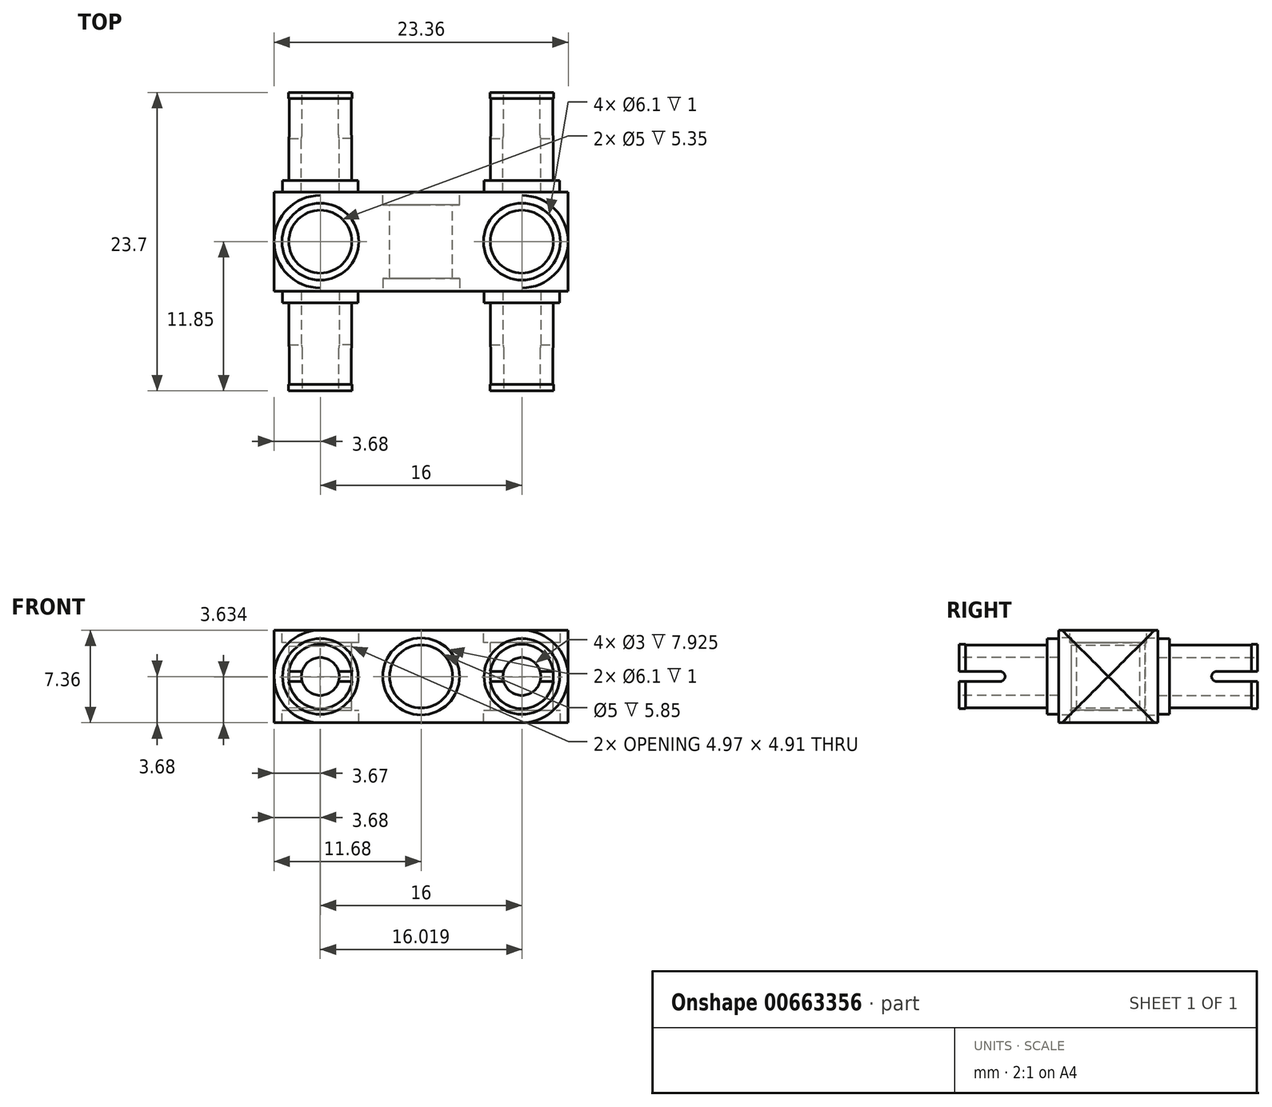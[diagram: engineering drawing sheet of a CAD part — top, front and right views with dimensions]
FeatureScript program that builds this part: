
annotation { "Feature Type Name" : "Feature", "Feature Type Description" : "" }
export const myFeature = defineFeature(function(context is Context, id is Id, definition is map)
    precondition{}
    {
        {
            var Q0;
            Q0=qCreatedBy(makeId("Front.planeOp"),FACE);
            var sketch = newSketch(context, id + "F0", { "sketchPlane" : qUnion([Q0])});
            skLineSegment(sketch, "E0.bottom", {"start": v(11.68, 3.67) * mm, "end": v(-11.68, 3.67) * mm});
            skLineSegment(sketch, "E0.top", {"start": v(11.68, -3.67) * mm, "end": v(-11.68, -3.67) * mm});
            skLineSegment(sketch, "E0.left", {"start": v(11.68, 3.67) * mm, "end": v(11.68, -3.67) * mm});
            skLineSegment(sketch, "E0.right", {"start": v(-11.68, 3.67) * mm, "end": v(-11.68, -3.67) * mm});
            skPoint(sketch, "E0.middle", {"position": v(0, 0) * mm});
            skCircle(sketch, "E1", {"center": v(-8, 0) * mm, "radius": 3.67 * mm});
            skCircle(sketch, "E2", {"center": v(8, 0) * mm, "radius": 3.67 * mm});
            skCircle(sketch, "E3", {"center": v(0, 0) * mm, "radius": 2.5 * mm});
            skCircle(sketch, "E4", {"center": v(0, 0) * mm, "radius": 3.05 * mm});
            skCircle(sketch, "E5", {"center": v(-8, 0) * mm, "radius": 3 * mm});
            skCircle(sketch, "E6", {"center": v(8, 0) * mm, "radius": 3 * mm});
            skCircle(sketch, "E7", {"center": v(-8, 0) * mm, "radius": 2.5 * mm});
            skCircle(sketch, "E8", {"center": v(8, 0) * mm, "radius": 2.5 * mm});
            skSolve(sketch);
        }
        {
            var Q0;
            Q0=makeQuery(id+"F0.imprint","IMPRINT",FACE,{"disambiguationData":[TD([[makeQuery(id+"F0.imprint","IMPRINT",EDGE,{"derivedFrom":sQuery(id+"F0.wireOp",EDGE,"E4")}),-1.0]])]});
            var Q1;
            {var subQ0=sQuery(id+"F0.wireOp",EDGE,"E1");var subQ1=makeQuery(id+"F0.imprint","INTERSECT",VERTEX,{"derivedFrom":[sQuery(id+"F0.wireOp",EDGE,"E0.bottom"),subQ0]});Q1=makeQuery(id+"F0.imprint","IMPRINT",FACE,{"disambiguationData":[TD([[makeQuery(id+"F0.imprint","IMPRINT",EDGE,{"disambiguationData":[TD([[subQ1,-1.0]])],"derivedFrom":subQ0}),1.0]])]});}
            var Q2;
            {var subQ0=sQuery(id+"F0.wireOp",EDGE,"E2");var subQ1=makeQuery(id+"F0.imprint","INTERSECT",VERTEX,{"derivedFrom":[sQuery(id+"F0.wireOp",EDGE,"E0.bottom"),subQ0]});Q2=makeQuery(id+"F0.imprint","IMPRINT",FACE,{"disambiguationData":[TD([[makeQuery(id+"F0.imprint","IMPRINT",EDGE,{"disambiguationData":[TD([[subQ1,1.0]])],"derivedFrom":subQ0}),1.0]])]});}
            var Q3;
            Q3=makeQuery(id+"F0.imprint","IMPRINT",FACE,{"disambiguationData":[TD([[makeQuery(id+"F0.imprint","IMPRINT",EDGE,{"derivedFrom":sQuery(id+"F0.wireOp",EDGE,"E3")}),-1.0]])]});
            extrude(context, id + "F1", {"entities" : qUnion([Q0, Q1, Q2, Q3]), "endBound" : BoundingType.SYMMETRIC, "depth" : 7.85 * mm, "offsetDistance" : 25 * mm});
        }
        {
            var Q0;
            Q0=makeQuery(id+"F0.imprint","IMPRINT",FACE,{"disambiguationData":[TD([[makeQuery(id+"F0.imprint","IMPRINT",EDGE,{"derivedFrom":sQuery(id+"F0.wireOp",EDGE,"E5")}),1.0]])]});
            var Q1;
            Q1=makeQuery(id+"F0.imprint","IMPRINT",FACE,{"disambiguationData":[TD([[makeQuery(id+"F0.imprint","IMPRINT",EDGE,{"derivedFrom":sQuery(id+"F0.wireOp",EDGE,"E6")}),1.0]])]});
            extrude(context, id + "F2", {"entities" : qUnion([Q0, Q1]), "operationType" : NewBodyOperationType.ADD, "endBound" : BoundingType.SYMMETRIC, "depth" : 9.7 * mm, "offsetDistance" : 25 * mm});
        }
        {
            var Q0;
            Q0=makeQuery(id+"F0.imprint","IMPRINT",FACE,{"disambiguationData":[TD([[makeQuery(id+"F0.imprint","IMPRINT",EDGE,{"derivedFrom":sQuery(id+"F0.wireOp",EDGE,"E7")}),1.0]])]});
            var Q1;
            Q1=makeQuery(id+"F0.imprint","IMPRINT",FACE,{"disambiguationData":[TD([[makeQuery(id+"F0.imprint","IMPRINT",EDGE,{"derivedFrom":sQuery(id+"F0.wireOp",EDGE,"E8")}),1.0]])]});
            extrude(context, id + "F3", {"entities" : qUnion([Q0, Q1]), "operationType" : NewBodyOperationType.ADD, "endBound" : BoundingType.SYMMETRIC, "depth" : 22.5 * mm, "offsetDistance" : 25 * mm});
        }
        {
            var Q0;
            Q0=makeQuery(id+"F3.opExtrude","CAP_FACE",FACE,{"disambiguationData":[OSD([sQuery(id+"F0.wireOp",EDGE,"E7")])],"isStart":false});
            var sketch = newSketch(context, id + "F4", { "sketchPlane" : qUnion([Q0])});
            skCircle(sketch, "E9", {"center": v(-8, 0) * mm, "radius": 2.55 * mm});
            skSolve(sketch);
        }
        {
            var Q0;
            Q0=qSketchRegion(id+"F4",true);
            extrude(context, id + "F5", {"entities" : qUnion([Q0]), "operationType" : NewBodyOperationType.ADD, "depth" : 0.6 * mm, "offsetDistance" : 25 * mm});
        }
        {
            var Q0;
            Q0=makeQuery(id+"F3.opExtrude","CAP_FACE",FACE,{"disambiguationData":[OSD([sQuery(id+"F0.wireOp",EDGE,"E8")])],"isStart":false});
            var sketch = newSketch(context, id + "F6", { "sketchPlane" : qUnion([Q0])});
            skCircle(sketch, "E10", {"center": v(8, 0) * mm, "radius": 2.55 * mm});
            skSolve(sketch);
        }
        {
            var Q0;
            Q0=qSketchRegion(id+"F6",true);
            extrude(context, id + "F7", {"entities" : qUnion([Q0]), "operationType" : NewBodyOperationType.ADD, "depth" : 0.6 * mm, "offsetDistance" : 25 * mm});
        }
        {
            var Q0;
            Q0=makeQuery(id+"F3.opExtrude","CAP_FACE",FACE,{"disambiguationData":[OSD([sQuery(id+"F0.wireOp",EDGE,"E7")])],"isStart":true});
            var sketch = newSketch(context, id + "F8", { "sketchPlane" : qUnion([Q0])});
            skCircle(sketch, "E11", {"center": v(8, 0) * mm, "radius": 2.55 * mm});
            skSolve(sketch);
        }
        {
            var Q0;
            Q0=qSketchRegion(id+"F8",true);
            extrude(context, id + "F9", {"entities" : qUnion([Q0]), "operationType" : NewBodyOperationType.ADD, "depth" : 0.6 * mm, "offsetDistance" : 25 * mm});
        }
        {
            var Q0;
            Q0=makeQuery(id+"F3.opExtrude","CAP_FACE",FACE,{"disambiguationData":[OSD([sQuery(id+"F0.wireOp",EDGE,"E8")])],"isStart":true});
            var sketch = newSketch(context, id + "F10", { "sketchPlane" : qUnion([Q0])});
            skCircle(sketch, "E12", {"center": v(-8, 0) * mm, "radius": 2.55 * mm});
            skSolve(sketch);
        }
        {
            var Q0;
            Q0=qSketchRegion(id+"F10",true);
            extrude(context, id + "F11", {"entities" : qUnion([Q0]), "operationType" : NewBodyOperationType.ADD, "depth" : 0.6 * mm, "offsetDistance" : 25 * mm});
        }
        {
            var Q0;
            Q0=makeQuery(id+"F9.opExtrude","CAP_FACE",FACE,{"disambiguationData":[OSD([sQuery(id+"F8.wireOp",EDGE,"E11")])],"isStart":false});
            var sketch = newSketch(context, id + "F12", { "sketchPlane" : qUnion([Q0])});
            skCircle(sketch, "E13", {"center": v(8, 0) * mm, "radius": 1.5 * mm});
            skSolve(sketch);
        }
        {
            var Q0;
            Q0=qSketchRegion(id+"F12",true);
            var Q1;
            Q1=makeQuery(id+"F1.opExtrude","CAP_FACE",FACE,{"disambiguationData":[OSD([sQuery(id+"F0.wireOp",EDGE,"E0.bottom"),sQuery(id+"F0.wireOp",EDGE,"E0.top"),sQuery(id+"F0.wireOp",EDGE,"E1"),sQuery(id+"F0.wireOp",EDGE,"E2"),sQuery(id+"F0.wireOp",EDGE,"E3"),sQuery(id+"F0.wireOp",EDGE,"E5"),sQuery(id+"F0.wireOp",EDGE,"E6")])],"isStart":true});
            extrude(context, id + "F13", {"entities" : qUnion([Q0]), "operationType" : NewBodyOperationType.REMOVE, "endBound" : BoundingType.UP_TO_SURFACE, "oppositeDirection" : true, "depth" : 25 * mm, "endBoundEntityFace" : qUnion([Q1]), "offsetDistance" : 25 * mm});
        }
        {
            var Q0;
            Q0=makeQuery(id+"F11.opExtrude","CAP_FACE",FACE,{"disambiguationData":[OSD([sQuery(id+"F10.wireOp",EDGE,"E12")])],"isStart":false});
            var sketch = newSketch(context, id + "F14", { "sketchPlane" : qUnion([Q0])});
            skCircle(sketch, "E14", {"center": v(-8, 0) * mm, "radius": 1.5 * mm});
            skSolve(sketch);
        }
        {
            var Q0;
            Q0=qSketchRegion(id+"F14",true);
            var Q1;
            Q1=makeQuery(id+"F1.opExtrude","CAP_FACE",FACE,{"disambiguationData":[OSD([sQuery(id+"F0.wireOp",EDGE,"E0.bottom"),sQuery(id+"F0.wireOp",EDGE,"E0.top"),sQuery(id+"F0.wireOp",EDGE,"E1"),sQuery(id+"F0.wireOp",EDGE,"E2"),sQuery(id+"F0.wireOp",EDGE,"E3"),sQuery(id+"F0.wireOp",EDGE,"E5"),sQuery(id+"F0.wireOp",EDGE,"E6")])],"isStart":true});
            extrude(context, id + "F15", {"entities" : qUnion([Q0]), "operationType" : NewBodyOperationType.REMOVE, "endBound" : BoundingType.UP_TO_SURFACE, "oppositeDirection" : true, "depth" : 25 * mm, "endBoundEntityFace" : qUnion([Q1]), "offsetDistance" : 25 * mm});
        }
        {
            var Q0;
            Q0=makeQuery(id+"F7.opExtrude","CAP_FACE",FACE,{"disambiguationData":[OSD([sQuery(id+"F6.wireOp",EDGE,"E10")])],"isStart":false});
            var sketch = newSketch(context, id + "F16", { "sketchPlane" : qUnion([Q0])});
            skCircle(sketch, "E15", {"center": v(8, 0) * mm, "radius": 1.5 * mm});
            skSolve(sketch);
        }
        {
            var Q0;
            Q0=qSketchRegion(id+"F16",true);
            var Q1;
            Q1=makeQuery(id+"F1.opExtrude","CAP_FACE",FACE,{"disambiguationData":[OSD([sQuery(id+"F0.wireOp",EDGE,"E0.bottom"),sQuery(id+"F0.wireOp",EDGE,"E0.top"),sQuery(id+"F0.wireOp",EDGE,"E1"),sQuery(id+"F0.wireOp",EDGE,"E2"),sQuery(id+"F0.wireOp",EDGE,"E3"),sQuery(id+"F0.wireOp",EDGE,"E5"),sQuery(id+"F0.wireOp",EDGE,"E6")])],"isStart":false});
            extrude(context, id + "F17", {"entities" : qUnion([Q0]), "operationType" : NewBodyOperationType.REMOVE, "endBound" : BoundingType.UP_TO_SURFACE, "oppositeDirection" : true, "depth" : 25 * mm, "endBoundEntityFace" : qUnion([Q1]), "offsetDistance" : 25 * mm});
        }
        {
            var Q0;
            Q0=makeQuery(id+"F5.opExtrude","CAP_FACE",FACE,{"disambiguationData":[OSD([sQuery(id+"F4.wireOp",EDGE,"E9")])],"isStart":false});
            var sketch = newSketch(context, id + "F18", { "sketchPlane" : qUnion([Q0])});
            skCircle(sketch, "E16", {"center": v(-8, 0) * mm, "radius": 1.5 * mm});
            skSolve(sketch);
        }
        {
            var Q0;
            Q0=qSketchRegion(id+"F18",true);
            var Q1;
            Q1=makeQuery(id+"F1.opExtrude","CAP_FACE",FACE,{"disambiguationData":[OSD([sQuery(id+"F0.wireOp",EDGE,"E0.bottom"),sQuery(id+"F0.wireOp",EDGE,"E0.top"),sQuery(id+"F0.wireOp",EDGE,"E1"),sQuery(id+"F0.wireOp",EDGE,"E2"),sQuery(id+"F0.wireOp",EDGE,"E3"),sQuery(id+"F0.wireOp",EDGE,"E5"),sQuery(id+"F0.wireOp",EDGE,"E6")])],"isStart":false});
            extrude(context, id + "F19", {"entities" : qUnion([Q0]), "operationType" : NewBodyOperationType.REMOVE, "endBound" : BoundingType.UP_TO_SURFACE, "oppositeDirection" : true, "depth" : 25 * mm, "endBoundEntityFace" : qUnion([Q1]), "offsetDistance" : 25 * mm});
        }
        {
            var Q0;
            Q0=makeQuery(id+"F1.opExtrude","SWEPT_FACE",FACE,{"disambiguationData":[OSD([sQuery(id+"F0.wireOp",EDGE,"E0.bottom")])]});
            var sketch = newSketch(context, id + "F20", { "sketchPlane" : qUnion([Q0])});
            skCircle(sketch, "E17", {"center": v(-8, 0) * mm, "radius": 3.67 * mm});
            skCircle(sketch, "E18", {"center": v(8, 0) * mm, "radius": 3.67 * mm});
            skCircle(sketch, "E19", {"center": v(-8, 0) * mm, "radius": 2.5 * mm});
            skCircle(sketch, "E20", {"center": v(8, 0) * mm, "radius": 2.5 * mm});
            skCircle(sketch, "E21", {"center": v(-8, 0) * mm, "radius": 3.05 * mm});
            skCircle(sketch, "E22", {"center": v(8, 0) * mm, "radius": 3.05 * mm});
            skSolve(sketch);
        }
        {
            var Q0;
            Q0=qSketchRegion(id+"F20",true);
            var Q1;
            Q1=makeQuery(id+"F1.opExtrude","SWEPT_FACE",FACE,{"disambiguationData":[OSD([sQuery(id+"F0.wireOp",EDGE,"E0.top")])]});
            extrude(context, id + "F21", {"entities" : qUnion([Q0]), "operationType" : NewBodyOperationType.ADD, "endBound" : BoundingType.UP_TO_SURFACE, "oppositeDirection" : true, "depth" : 25 * mm, "endBoundEntityFace" : qUnion([Q1]), "offsetDistance" : 25 * mm});
        }
        {
            var Q0;
            {var subQ0=sQuery(id+"F20.wireOp",EDGE,"E19");var subQ1=makeQuery(id+"F1.opExtrude","SWEPT_EDGE",EDGE,{"disambiguationData":[OSD([sQuery(id+"F0.wireOp",EDGE,"E0.bottom"),sQuery(id+"F0.wireOp",EDGE,"E1")])]});var subQ2=makeQuery(id+"F20.imprint","INTERSECT",VERTEX,{"disambiguationData":[OD(0.0)],"derivedFrom":[subQ1,subQ0]});Q0=makeQuery(id+"F20.imprint","IMPRINT",FACE,{"disambiguationData":[TD([[makeQuery(id+"F20.imprint","IMPRINT",EDGE,{"disambiguationData":[TD([[subQ2,-1.0]])],"derivedFrom":subQ0}),1.0]])]});}
            var Q1;
            {var subQ0=sQuery(id+"F20.wireOp",EDGE,"E19");var subQ1=makeQuery(id+"F1.opExtrude","SWEPT_EDGE",EDGE,{"disambiguationData":[OSD([sQuery(id+"F0.wireOp",EDGE,"E0.bottom"),sQuery(id+"F0.wireOp",EDGE,"E1")])]});var subQ2=makeQuery(id+"F20.imprint","INTERSECT",VERTEX,{"disambiguationData":[OD(0.0)],"derivedFrom":[subQ1,subQ0]});Q1=makeQuery(id+"F20.imprint","IMPRINT",FACE,{"disambiguationData":[TD([[makeQuery(id+"F20.imprint","IMPRINT",EDGE,{"disambiguationData":[TD([[subQ2,1.0]])],"derivedFrom":subQ0}),1.0]])]});}
            var Q2;
            {var subQ0=sQuery(id+"F20.wireOp",EDGE,"E20");var subQ1=makeQuery(id+"F1.opExtrude","SWEPT_EDGE",EDGE,{"disambiguationData":[OSD([sQuery(id+"F0.wireOp",EDGE,"E0.bottom"),sQuery(id+"F0.wireOp",EDGE,"E2")])]});var subQ2=makeQuery(id+"F20.imprint","INTERSECT",VERTEX,{"disambiguationData":[OD(0.0)],"derivedFrom":[subQ1,subQ0]});Q2=makeQuery(id+"F20.imprint","IMPRINT",FACE,{"disambiguationData":[TD([[makeQuery(id+"F20.imprint","IMPRINT",EDGE,{"disambiguationData":[TD([[subQ2,-1.0]])],"derivedFrom":subQ0}),1.0]])]});}
            var Q3;
            {var subQ0=sQuery(id+"F20.wireOp",EDGE,"E20");var subQ1=makeQuery(id+"F1.opExtrude","SWEPT_EDGE",EDGE,{"disambiguationData":[OSD([sQuery(id+"F0.wireOp",EDGE,"E0.bottom"),sQuery(id+"F0.wireOp",EDGE,"E2")])]});var subQ2=makeQuery(id+"F20.imprint","INTERSECT",VERTEX,{"disambiguationData":[OD(0.0)],"derivedFrom":[subQ1,subQ0]});Q3=makeQuery(id+"F20.imprint","IMPRINT",FACE,{"disambiguationData":[TD([[makeQuery(id+"F20.imprint","IMPRINT",EDGE,{"disambiguationData":[TD([[subQ2,1.0]])],"derivedFrom":subQ0}),1.0]])]});}
            extrude(context, id + "F22", {"entities" : qUnion([Q0, Q1, Q2, Q3]), "operationType" : NewBodyOperationType.REMOVE, "endBound" : BoundingType.THROUGH_ALL, "oppositeDirection" : true, "depth" : 25 * mm, "offsetDistance" : 25 * mm});
        }
        {
            var Q0;
            {var subQ0=sQuery(id+"F20.wireOp",EDGE,"E19");var subQ1=makeQuery(id+"F1.opExtrude","SWEPT_EDGE",EDGE,{"disambiguationData":[OSD([sQuery(id+"F0.wireOp",EDGE,"E0.bottom"),sQuery(id+"F0.wireOp",EDGE,"E1")])]});var subQ2=makeQuery(id+"F20.imprint","INTERSECT",VERTEX,{"disambiguationData":[OD(0.0)],"derivedFrom":[subQ1,subQ0]});Q0=makeQuery(id+"F20.imprint","IMPRINT",FACE,{"disambiguationData":[TD([[makeQuery(id+"F20.imprint","IMPRINT",EDGE,{"disambiguationData":[TD([[subQ2,1.0]])],"derivedFrom":subQ0}),-1.0]])]});}
            var Q1;
            {var subQ0=sQuery(id+"F20.wireOp",EDGE,"E20");var subQ1=makeQuery(id+"F1.opExtrude","SWEPT_EDGE",EDGE,{"disambiguationData":[OSD([sQuery(id+"F0.wireOp",EDGE,"E0.bottom"),sQuery(id+"F0.wireOp",EDGE,"E2")])]});var subQ2=makeQuery(id+"F20.imprint","INTERSECT",VERTEX,{"disambiguationData":[OD(0.0)],"derivedFrom":[subQ1,subQ0]});Q1=makeQuery(id+"F20.imprint","IMPRINT",FACE,{"disambiguationData":[TD([[makeQuery(id+"F20.imprint","IMPRINT",EDGE,{"disambiguationData":[TD([[subQ2,-1.0]])],"derivedFrom":subQ0}),-1.0]])]});}
            var Q2;
            {var subQ0=sQuery(id+"F20.wireOp",EDGE,"E20");var subQ1=makeQuery(id+"F1.opExtrude","SWEPT_EDGE",EDGE,{"disambiguationData":[OSD([sQuery(id+"F0.wireOp",EDGE,"E0.bottom"),sQuery(id+"F0.wireOp",EDGE,"E2")])]});var subQ2=makeQuery(id+"F20.imprint","INTERSECT",VERTEX,{"disambiguationData":[OD(0.0)],"derivedFrom":[subQ1,subQ0]});Q2=makeQuery(id+"F20.imprint","IMPRINT",FACE,{"disambiguationData":[TD([[makeQuery(id+"F20.imprint","IMPRINT",EDGE,{"disambiguationData":[TD([[subQ2,1.0]])],"derivedFrom":subQ0}),-1.0]])]});}
            var Q3;
            {var subQ0=sQuery(id+"F20.wireOp",EDGE,"E19");var subQ1=makeQuery(id+"F1.opExtrude","SWEPT_EDGE",EDGE,{"disambiguationData":[OSD([sQuery(id+"F0.wireOp",EDGE,"E0.bottom"),sQuery(id+"F0.wireOp",EDGE,"E1")])]});var subQ2=makeQuery(id+"F20.imprint","INTERSECT",VERTEX,{"disambiguationData":[OD(0.0)],"derivedFrom":[subQ1,subQ0]});Q3=makeQuery(id+"F20.imprint","IMPRINT",FACE,{"disambiguationData":[TD([[makeQuery(id+"F20.imprint","IMPRINT",EDGE,{"disambiguationData":[TD([[subQ2,-1.0]])],"derivedFrom":subQ0}),-1.0]])]});}
            extrude(context, id + "F23", {"entities" : qUnion([Q0, Q1, Q2, Q3]), "operationType" : NewBodyOperationType.REMOVE, "oppositeDirection" : true, "depth" : 1 * mm, "offsetDistance" : 25 * mm});
        }
        {
            var Q0;
            {var subQ0=sQuery(id+"F0.wireOp",EDGE,"E0.top");Q0=makeQuery(id+"F21.boolean.opBoolean","MERGE",FACE,{"derivedFrom":[makeQuery(id+"F1.opExtrude","SWEPT_FACE",FACE,{"disambiguationData":[OSD([subQ0])]}),makeQuery(id+"F21.opExtrude","CAP_FACE",FACE,{"disambiguationData":[OSD([subQ0]),OD(0.0)],"isStart":false}),makeQuery(id+"F21.opExtrude","CAP_FACE",FACE,{"disambiguationData":[OSD([subQ0]),OD(1.0)],"isStart":false})]});}
            var sketch = newSketch(context, id + "F24", { "sketchPlane" : qUnion([Q0])});
            skCircle(sketch, "E23", {"center": v(-8, 0) * mm, "radius": 3.05 * mm});
            skCircle(sketch, "E24", {"center": v(-8, 0) * mm, "radius": 2.5 * mm});
            skCircle(sketch, "E25", {"center": v(8, 0) * mm, "radius": 2.5 * mm});
            skCircle(sketch, "E26", {"center": v(8, 0) * mm, "radius": 3.05 * mm});
            skSolve(sketch);
        }
        {
            var Q0;
            Q0=makeQuery(id+"F24.imprint","IMPRINT",FACE,{"disambiguationData":[TD([[makeQuery(id+"F24.imprint","IMPRINT",EDGE,{"disambiguationData":[OD(0.0)],"derivedFrom":sQuery(id+"F24.wireOp",EDGE,"E26")}),1.0]])]});
            var Q1;
            Q1=makeQuery(id+"F24.imprint","IMPRINT",FACE,{"disambiguationData":[TD([[makeQuery(id+"F24.imprint","IMPRINT",EDGE,{"disambiguationData":[OD(1.0)],"derivedFrom":sQuery(id+"F24.wireOp",EDGE,"E26")}),-1.0]])]});
            var Q2;
            Q2=makeQuery(id+"F24.imprint","IMPRINT",FACE,{"disambiguationData":[TD([[makeQuery(id+"F24.imprint","IMPRINT",EDGE,{"disambiguationData":[OD(1.0)],"derivedFrom":sQuery(id+"F24.wireOp",EDGE,"E23")}),-1.0]])]});
            var Q3;
            Q3=makeQuery(id+"F24.imprint","IMPRINT",FACE,{"disambiguationData":[TD([[makeQuery(id+"F24.imprint","IMPRINT",EDGE,{"disambiguationData":[OD(0.0)],"derivedFrom":sQuery(id+"F24.wireOp",EDGE,"E23")}),1.0]])]});
            extrude(context, id + "F25", {"entities" : qUnion([Q0, Q1, Q2, Q3]), "operationType" : NewBodyOperationType.REMOVE, "oppositeDirection" : true, "depth" : 1 * mm, "offsetDistance" : 25 * mm});
        }
        {
            var Q0;
            Q0=makeQuery(id+"F1.opExtrude","CAP_FACE",FACE,{"disambiguationData":[OSD([sQuery(id+"F0.wireOp",EDGE,"E0.bottom"),sQuery(id+"F0.wireOp",EDGE,"E0.top"),sQuery(id+"F0.wireOp",EDGE,"E1"),sQuery(id+"F0.wireOp",EDGE,"E2"),sQuery(id+"F0.wireOp",EDGE,"E3"),sQuery(id+"F0.wireOp",EDGE,"E5"),sQuery(id+"F0.wireOp",EDGE,"E6")])],"isStart":true});
            var sketch = newSketch(context, id + "F26", { "sketchPlane" : qUnion([Q0])});
            skCircle(sketch, "E27", {"center": v(0, 0) * mm, "radius": 3.05 * mm});
            skSolve(sketch);
        }
        {
            var Q0;
            Q0=makeQuery(id+"F26.imprint","IMPRINT",FACE,{"disambiguationData":[TD([[makeQuery(id+"F26.imprint","IMPRINT",EDGE,{"derivedFrom":sQuery(id+"F26.wireOp",EDGE,"E27")}),1.0]])]});
            extrude(context, id + "F27", {"entities" : qUnion([Q0]), "operationType" : NewBodyOperationType.REMOVE, "oppositeDirection" : true, "depth" : 1 * mm, "offsetDistance" : 25 * mm});
        }
        {
            var Q0;
            Q0=makeQuery(id+"F1.opExtrude","CAP_FACE",FACE,{"disambiguationData":[OSD([sQuery(id+"F0.wireOp",EDGE,"E0.bottom"),sQuery(id+"F0.wireOp",EDGE,"E0.top"),sQuery(id+"F0.wireOp",EDGE,"E1"),sQuery(id+"F0.wireOp",EDGE,"E2"),sQuery(id+"F0.wireOp",EDGE,"E3"),sQuery(id+"F0.wireOp",EDGE,"E5"),sQuery(id+"F0.wireOp",EDGE,"E6")])],"isStart":false});
            var sketch = newSketch(context, id + "F28", { "sketchPlane" : qUnion([Q0])});
            skCircle(sketch, "E28", {"center": v(0, 0) * mm, "radius": 3.05 * mm});
            skSolve(sketch);
        }
        {
            var Q0;
            Q0=makeQuery(id+"F28.imprint","IMPRINT",FACE,{"disambiguationData":[TD([[makeQuery(id+"F28.imprint","IMPRINT",EDGE,{"derivedFrom":sQuery(id+"F28.wireOp",EDGE,"E28")}),1.0]])]});
            extrude(context, id + "F29", {"entities" : qUnion([Q0]), "operationType" : NewBodyOperationType.REMOVE, "oppositeDirection" : true, "depth" : 1 * mm, "offsetDistance" : 25 * mm});
        }
        {
            var Q0;
            Q0=makeQuery(id+"F23.boolean.opBoolean","COPY",FACE,{"derivedFrom":makeQuery(id+"F23.opExtrude","CAP_FACE",FACE,{"disambiguationData":[OSD([sQuery(id+"F20.wireOp",EDGE,"E20"),sQuery(id+"F20.wireOp",EDGE,"E22")])],"isStart":false})});
            var sketch = newSketch(context, id + "F30", { "sketchPlane" : qUnion([Q0])});
            skCircle(sketch, "E29", {"center": v(8, 0) * mm, "radius": 3.05 * mm});
            skCircle(sketch, "E30", {"center": v(8, 0) * mm, "radius": 2.5 * mm});
            skSolve(sketch);
        }
        {
            var Q0;
            Q0=makeQuery(id+"F30.imprint","IMPRINT",FACE,{"disambiguationData":[TD([[makeQuery(id+"F30.imprint","IMPRINT",EDGE,{"derivedFrom":sQuery(id+"F30.wireOp",EDGE,"E30")}),-1.0]])]});
            var Q1;
            {var subQ1=sQuery(id+"F20.wireOp",EDGE,"E22");var subQ2=makeQuery(id+"F23.boolean.opBoolean","INTERSECT",EDGE,{"derivedFrom":[makeQuery(id+"F21.boolean.opBoolean","SPLIT",FACE,{"disambiguationData":[TD([makeQuery(id+"F1.opExtrude","SWEPT_FACE",FACE,{"disambiguationData":[OSD([sQuery(id+"F0.wireOp",EDGE,"E0.bottom")])]}),makeQuery(id+"F21.opExtrude","CAP_FACE",FACE,{"disambiguationData":[OSD([sQuery(id+"F20.wireOp",EDGE,"E17"),sQuery(id+"F20.wireOp",EDGE,"E21")])],"isStart":true}),makeQuery(id+"F21.opExtrude","CAP_FACE",FACE,{"disambiguationData":[OSD([sQuery(id+"F20.wireOp",EDGE,"E18"),subQ1])],"isStart":true}),makeQuery(id+"F21.opExtrude","SWEPT_FACE",FACE,{"disambiguationData":[OSD([subQ1])]})])],"derivedFrom":makeQuery(id+"F1.opExtrude","SWEPT_FACE",FACE,{"disambiguationData":[OSD([sQuery(id+"F0.wireOp",EDGE,"E2")])]})}),makeQuery(id+"F23.opExtrude","CAP_FACE",FACE,{"disambiguationData":[OSD([sQuery(id+"F20.wireOp",EDGE,"E20"),subQ1])],"isStart":false})]});Q1=makeQuery(id+"F30.imprint","IMPRINT",FACE,{"disambiguationData":[TD([[makeQuery(id+"F30.imprint","IMPRINT",EDGE,{"derivedFrom":subQ2}),-1.0]])]});}
            var Q2;
            Q2=makeQuery(id+"F25.boolean.opBoolean","COPY",FACE,{"derivedFrom":makeQuery(id+"F25.opExtrude","CAP_FACE",FACE,{"disambiguationData":[OSD([sQuery(id+"F24.wireOp",EDGE,"E25"),sQuery(id+"F24.wireOp",EDGE,"E26")])],"isStart":false})});
            extrude(context, id + "F31", {"entities" : qUnion([Q0, Q1]), "operationType" : NewBodyOperationType.ADD, "endBound" : BoundingType.UP_TO_SURFACE, "oppositeDirection" : true, "depth" : 25 * mm, "endBoundEntityFace" : qUnion([Q2]), "offsetDistance" : 25 * mm});
        }
        {
            var Q0;
            Q0=makeQuery(id+"F23.boolean.opBoolean","COPY",FACE,{"derivedFrom":makeQuery(id+"F23.opExtrude","CAP_FACE",FACE,{"disambiguationData":[OSD([sQuery(id+"F20.wireOp",EDGE,"E19"),sQuery(id+"F20.wireOp",EDGE,"E21")])],"isStart":false})});
            var sketch = newSketch(context, id + "F32", { "sketchPlane" : qUnion([Q0])});
            skCircle(sketch, "E31", {"center": v(-8, 0) * mm, "radius": 3.05 * mm});
            skCircle(sketch, "E32", {"center": v(-8, 0) * mm, "radius": 2.5 * mm});
            skSolve(sketch);
        }
        {
            var Q0;
            Q0=makeQuery(id+"F32.imprint","IMPRINT",FACE,{"disambiguationData":[TD([[makeQuery(id+"F32.imprint","IMPRINT",EDGE,{"derivedFrom":sQuery(id+"F32.wireOp",EDGE,"E32")}),-1.0]])]});
            var Q1;
            {var subQ1=sQuery(id+"F20.wireOp",EDGE,"E21");var subQ2=makeQuery(id+"F23.boolean.opBoolean","INTERSECT",EDGE,{"derivedFrom":[makeQuery(id+"F21.boolean.opBoolean","SPLIT",FACE,{"disambiguationData":[TD([makeQuery(id+"F1.opExtrude","SWEPT_FACE",FACE,{"disambiguationData":[OSD([sQuery(id+"F0.wireOp",EDGE,"E0.bottom")])]}),makeQuery(id+"F21.opExtrude","CAP_FACE",FACE,{"disambiguationData":[OSD([sQuery(id+"F20.wireOp",EDGE,"E17"),subQ1])],"isStart":true}),makeQuery(id+"F21.opExtrude","CAP_FACE",FACE,{"disambiguationData":[OSD([sQuery(id+"F20.wireOp",EDGE,"E18"),sQuery(id+"F20.wireOp",EDGE,"E22")])],"isStart":true}),makeQuery(id+"F21.opExtrude","SWEPT_FACE",FACE,{"disambiguationData":[OSD([subQ1])]})])],"derivedFrom":makeQuery(id+"F1.opExtrude","SWEPT_FACE",FACE,{"disambiguationData":[OSD([sQuery(id+"F0.wireOp",EDGE,"E1")])]})}),makeQuery(id+"F23.opExtrude","CAP_FACE",FACE,{"disambiguationData":[OSD([sQuery(id+"F20.wireOp",EDGE,"E19"),subQ1])],"isStart":false})]});Q1=makeQuery(id+"F32.imprint","IMPRINT",FACE,{"disambiguationData":[TD([[makeQuery(id+"F32.imprint","IMPRINT",EDGE,{"derivedFrom":subQ2}),-1.0]])]});}
            var Q2;
            Q2=makeQuery(id+"F25.boolean.opBoolean","COPY",FACE,{"derivedFrom":makeQuery(id+"F25.opExtrude","CAP_FACE",FACE,{"disambiguationData":[OSD([sQuery(id+"F24.wireOp",EDGE,"E23"),sQuery(id+"F24.wireOp",EDGE,"E24")])],"isStart":false})});
            extrude(context, id + "F33", {"entities" : qUnion([Q0, Q1]), "operationType" : NewBodyOperationType.ADD, "endBound" : BoundingType.UP_TO_SURFACE, "oppositeDirection" : true, "depth" : 25 * mm, "endBoundEntityFace" : qUnion([Q2]), "offsetDistance" : 25 * mm});
        }
        {
            var Q0;
            Q0=qCreatedBy(makeId("Right.planeOp"),FACE);
            var sketch = newSketch(context, id + "F34", { "sketchPlane" : qUnion([Q0])});
            skLineSegment(sketch, "E33", {"start": v(0, 0) * mm, "end": v(8.2, 0) * mm, "construction": true});
            skLineSegment(sketch, "E34", {"start": v(0, 0) * mm, "end": v(-8.2, 0) * mm, "construction": true});
            skLineSegment(sketch, "E35.bottom", {"start": v(-8.2, 0.4) * mm, "end": v(-11.85, 0.4) * mm});
            skLineSegment(sketch, "E35.top", {"start": v(-8.2, -0.4) * mm, "end": v(-11.85, -0.4) * mm});
            skLineSegment(sketch, "E35.left", {"start": v(-8.2, 0.4) * mm, "end": v(-8.2, -0.4) * mm});
            skPoint(sketch, "E35.middle", {"position": v(-12.33, 0) * mm});
            skLineSegment(sketch, "E36.bottom", {"start": v(8.2, -0.4) * mm, "end": v(11.85, -0.4) * mm});
            skLineSegment(sketch, "E36.top", {"start": v(8.2, 0.4) * mm, "end": v(11.85, 0.4) * mm});
            skLineSegment(sketch, "E36.left", {"start": v(8.2, -0.4) * mm, "end": v(8.2, 0.4) * mm});
            skPoint(sketch, "E36.middle", {"position": v(15.2, 0) * mm});
            skPoint(sketch, "E36.middle.positionSnap0", {"position": v(-4.1, 0) * mm});
            skPoint(sketch, "E36.centerSnap0", {"position": v(-4.1, 0) * mm});
            skLineSegment(sketch, "E37", {"start": v(-11.85, 0.4) * mm, "end": v(-11.85, -0.4) * mm});
            skLineSegment(sketch, "E38", {"start": v(11.85, 0.4) * mm, "end": v(11.85, -0.4) * mm});
            skPoint(sketch, "E36.right.end.orphan", {"position": v(22.18, 0.4) * mm});
            skPoint(sketch, "E36.right.start.orphan", {"position": v(22.18, -0.4) * mm});
            skPoint(sketch, "E39.orphan", {"position": v(-16.46, 0.4) * mm});
            skPoint(sketch, "E40.orphan", {"position": v(-16.46, -0.4) * mm});
            skSolve(sketch);
        }
        {
            var Q0;
            Q0=makeQuery(id+"F34.imprint","IMPRINT",FACE,{"disambiguationData":[TD([[makeQuery(id+"F34.imprint","IMPRINT",EDGE,{"derivedFrom":sQuery(id+"F34.wireOp",EDGE,"E36.bottom")}),1.0]])]});
            var Q1;
            Q1=makeQuery(id+"F34.imprint","IMPRINT",FACE,{"disambiguationData":[TD([[makeQuery(id+"F34.imprint","IMPRINT",EDGE,{"derivedFrom":sQuery(id+"F34.wireOp",EDGE,"E35.bottom")}),1.0]])]});
            extrude(context, id + "F35", {"entities" : qUnion([Q0, Q1]), "operationType" : NewBodyOperationType.REMOVE, "endBound" : BoundingType.SYMMETRIC, "oppositeDirection" : true, "depth" : 25 * mm, "offsetDistance" : 25 * mm});
        }
        {
            var Q0;
            {var subQ0=sQuery(id+"F34.wireOp",EDGE,"E36.bottom");var subQ1=sQuery(id+"F34.wireOp",EDGE,"E36.left");Q0=makeQuery(id+"F35.boolean.opBoolean","COPY",EDGE,{"disambiguationData":[TD([makeQuery(id+"F3.opExtrude","SWEPT_FACE",FACE,{"disambiguationData":[OSD([sQuery(id+"F0.wireOp",EDGE,"E8")])]}),makeQuery(id+"F15.boolean.opBoolean","COPY",FACE,{"derivedFrom":makeQuery(id+"F15.opExtrude","SWEPT_FACE",FACE,{"disambiguationData":[OSD([sQuery(id+"F14.wireOp",EDGE,"E14")])]})}),makeQuery(id+"F35.opExtrude","SWEPT_FACE",FACE,{"disambiguationData":[OSD([subQ0])]}),makeQuery(id+"F35.opExtrude","SWEPT_FACE",FACE,{"disambiguationData":[OSD([subQ1])]})]),OD(1.0)],"derivedFrom":makeQuery(id+"F35.opExtrude","SWEPT_EDGE",EDGE,{"disambiguationData":[OSD([subQ0,subQ1])]})});}
            var Q1;
            {var subQ0=sQuery(id+"F34.wireOp",EDGE,"E36.top");var subQ1=sQuery(id+"F34.wireOp",EDGE,"E36.left");Q1=makeQuery(id+"F35.boolean.opBoolean","COPY",EDGE,{"disambiguationData":[TD([makeQuery(id+"F3.opExtrude","SWEPT_FACE",FACE,{"disambiguationData":[OSD([sQuery(id+"F0.wireOp",EDGE,"E8")])]}),makeQuery(id+"F15.boolean.opBoolean","COPY",FACE,{"derivedFrom":makeQuery(id+"F15.opExtrude","SWEPT_FACE",FACE,{"disambiguationData":[OSD([sQuery(id+"F14.wireOp",EDGE,"E14")])]})}),makeQuery(id+"F35.opExtrude","SWEPT_FACE",FACE,{"disambiguationData":[OSD([subQ0])]}),makeQuery(id+"F35.opExtrude","SWEPT_FACE",FACE,{"disambiguationData":[OSD([subQ1])]})]),OD(1.0)],"derivedFrom":makeQuery(id+"F35.opExtrude","SWEPT_EDGE",EDGE,{"disambiguationData":[OSD([subQ0,subQ1])]})});}
            var Q2;
            {var subQ0=sQuery(id+"F34.wireOp",EDGE,"E36.top");var subQ1=sQuery(id+"F34.wireOp",EDGE,"E36.left");Q2=makeQuery(id+"F35.boolean.opBoolean","COPY",EDGE,{"disambiguationData":[TD([makeQuery(id+"F3.opExtrude","SWEPT_FACE",FACE,{"disambiguationData":[OSD([sQuery(id+"F0.wireOp",EDGE,"E7")])]}),makeQuery(id+"F13.boolean.opBoolean","COPY",FACE,{"derivedFrom":makeQuery(id+"F13.opExtrude","SWEPT_FACE",FACE,{"disambiguationData":[OSD([sQuery(id+"F12.wireOp",EDGE,"E13")])]})}),makeQuery(id+"F35.opExtrude","SWEPT_FACE",FACE,{"disambiguationData":[OSD([subQ0])]}),makeQuery(id+"F35.opExtrude","SWEPT_FACE",FACE,{"disambiguationData":[OSD([subQ1])]})]),OD(1.0)],"derivedFrom":makeQuery(id+"F35.opExtrude","SWEPT_EDGE",EDGE,{"disambiguationData":[OSD([subQ0,subQ1])]})});}
            var Q3;
            {var subQ0=sQuery(id+"F34.wireOp",EDGE,"E35.bottom");var subQ1=sQuery(id+"F34.wireOp",EDGE,"E35.left");Q3=makeQuery(id+"F35.boolean.opBoolean","COPY",EDGE,{"disambiguationData":[TD([makeQuery(id+"F3.opExtrude","SWEPT_FACE",FACE,{"disambiguationData":[OSD([sQuery(id+"F0.wireOp",EDGE,"E8")])]}),makeQuery(id+"F17.boolean.opBoolean","COPY",FACE,{"derivedFrom":makeQuery(id+"F17.opExtrude","SWEPT_FACE",FACE,{"disambiguationData":[OSD([sQuery(id+"F16.wireOp",EDGE,"E15")])]})}),makeQuery(id+"F35.opExtrude","SWEPT_FACE",FACE,{"disambiguationData":[OSD([subQ0])]}),makeQuery(id+"F35.opExtrude","SWEPT_FACE",FACE,{"disambiguationData":[OSD([subQ1])]})]),OD(1.0)],"derivedFrom":makeQuery(id+"F35.opExtrude","SWEPT_EDGE",EDGE,{"disambiguationData":[OSD([subQ0,subQ1])]})});}
            var Q4;
            {var subQ0=sQuery(id+"F34.wireOp",EDGE,"E36.bottom");var subQ1=sQuery(id+"F34.wireOp",EDGE,"E36.left");Q4=makeQuery(id+"F35.boolean.opBoolean","COPY",EDGE,{"disambiguationData":[TD([makeQuery(id+"F3.opExtrude","SWEPT_FACE",FACE,{"disambiguationData":[OSD([sQuery(id+"F0.wireOp",EDGE,"E7")])]}),makeQuery(id+"F13.boolean.opBoolean","COPY",FACE,{"derivedFrom":makeQuery(id+"F13.opExtrude","SWEPT_FACE",FACE,{"disambiguationData":[OSD([sQuery(id+"F12.wireOp",EDGE,"E13")])]})}),makeQuery(id+"F35.opExtrude","SWEPT_FACE",FACE,{"disambiguationData":[OSD([subQ0])]}),makeQuery(id+"F35.opExtrude","SWEPT_FACE",FACE,{"disambiguationData":[OSD([subQ1])]})]),OD(1.0)],"derivedFrom":makeQuery(id+"F35.opExtrude","SWEPT_EDGE",EDGE,{"disambiguationData":[OSD([subQ0,subQ1])]})});}
            var Q5;
            {var subQ0=sQuery(id+"F34.wireOp",EDGE,"E35.top");var subQ1=sQuery(id+"F34.wireOp",EDGE,"E35.left");Q5=makeQuery(id+"F35.boolean.opBoolean","COPY",EDGE,{"disambiguationData":[TD([makeQuery(id+"F3.opExtrude","SWEPT_FACE",FACE,{"disambiguationData":[OSD([sQuery(id+"F0.wireOp",EDGE,"E8")])]}),makeQuery(id+"F17.boolean.opBoolean","COPY",FACE,{"derivedFrom":makeQuery(id+"F17.opExtrude","SWEPT_FACE",FACE,{"disambiguationData":[OSD([sQuery(id+"F16.wireOp",EDGE,"E15")])]})}),makeQuery(id+"F35.opExtrude","SWEPT_FACE",FACE,{"disambiguationData":[OSD([subQ0])]}),makeQuery(id+"F35.opExtrude","SWEPT_FACE",FACE,{"disambiguationData":[OSD([subQ1])]})]),OD(1.0)],"derivedFrom":makeQuery(id+"F35.opExtrude","SWEPT_EDGE",EDGE,{"disambiguationData":[OSD([subQ0,subQ1])]})});}
            var Q6;
            {var subQ0=sQuery(id+"F34.wireOp",EDGE,"E35.left");var subQ1=sQuery(id+"F34.wireOp",EDGE,"E35.top");Q6=makeQuery(id+"F35.boolean.opBoolean","COPY",EDGE,{"disambiguationData":[TD([makeQuery(id+"F3.opExtrude","SWEPT_FACE",FACE,{"disambiguationData":[OSD([sQuery(id+"F0.wireOp",EDGE,"E7")])]}),makeQuery(id+"F19.boolean.opBoolean","COPY",FACE,{"derivedFrom":makeQuery(id+"F19.opExtrude","SWEPT_FACE",FACE,{"disambiguationData":[OSD([sQuery(id+"F18.wireOp",EDGE,"E16")])]})}),makeQuery(id+"F35.opExtrude","SWEPT_FACE",FACE,{"disambiguationData":[OSD([subQ1])]}),makeQuery(id+"F35.opExtrude","SWEPT_FACE",FACE,{"disambiguationData":[OSD([subQ0])]})]),OD(1.0)],"derivedFrom":makeQuery(id+"F35.opExtrude","SWEPT_EDGE",EDGE,{"disambiguationData":[OSD([subQ1,subQ0])]})});}
            var Q7;
            {var subQ0=sQuery(id+"F34.wireOp",EDGE,"E35.bottom");var subQ1=sQuery(id+"F34.wireOp",EDGE,"E35.left");Q7=makeQuery(id+"F35.boolean.opBoolean","COPY",EDGE,{"disambiguationData":[TD([makeQuery(id+"F3.opExtrude","SWEPT_FACE",FACE,{"disambiguationData":[OSD([sQuery(id+"F0.wireOp",EDGE,"E7")])]}),makeQuery(id+"F19.boolean.opBoolean","COPY",FACE,{"derivedFrom":makeQuery(id+"F19.opExtrude","SWEPT_FACE",FACE,{"disambiguationData":[OSD([sQuery(id+"F18.wireOp",EDGE,"E16")])]})}),makeQuery(id+"F35.opExtrude","SWEPT_FACE",FACE,{"disambiguationData":[OSD([subQ0])]}),makeQuery(id+"F35.opExtrude","SWEPT_FACE",FACE,{"disambiguationData":[OSD([subQ1])]})]),OD(1.0)],"derivedFrom":makeQuery(id+"F35.opExtrude","SWEPT_EDGE",EDGE,{"disambiguationData":[OSD([subQ0,subQ1])]})});}
            var Q8;
            {var subQ0=sQuery(id+"F34.wireOp",EDGE,"E35.bottom");var subQ1=sQuery(id+"F34.wireOp",EDGE,"E35.left");Q8=makeQuery(id+"F35.boolean.opBoolean","COPY",EDGE,{"disambiguationData":[TD([makeQuery(id+"F3.opExtrude","SWEPT_FACE",FACE,{"disambiguationData":[OSD([sQuery(id+"F0.wireOp",EDGE,"E7")])]}),makeQuery(id+"F19.boolean.opBoolean","COPY",FACE,{"derivedFrom":makeQuery(id+"F19.opExtrude","SWEPT_FACE",FACE,{"disambiguationData":[OSD([sQuery(id+"F18.wireOp",EDGE,"E16")])]})}),makeQuery(id+"F35.opExtrude","SWEPT_FACE",FACE,{"disambiguationData":[OSD([subQ0])]}),makeQuery(id+"F35.opExtrude","SWEPT_FACE",FACE,{"disambiguationData":[OSD([subQ1])]})]),OD(0.0)],"derivedFrom":makeQuery(id+"F35.opExtrude","SWEPT_EDGE",EDGE,{"disambiguationData":[OSD([subQ0,subQ1])]})});}
            var Q9;
            {var subQ0=sQuery(id+"F34.wireOp",EDGE,"E35.left");var subQ1=sQuery(id+"F34.wireOp",EDGE,"E35.top");Q9=makeQuery(id+"F35.boolean.opBoolean","COPY",EDGE,{"disambiguationData":[TD([makeQuery(id+"F3.opExtrude","SWEPT_FACE",FACE,{"disambiguationData":[OSD([sQuery(id+"F0.wireOp",EDGE,"E7")])]}),makeQuery(id+"F19.boolean.opBoolean","COPY",FACE,{"derivedFrom":makeQuery(id+"F19.opExtrude","SWEPT_FACE",FACE,{"disambiguationData":[OSD([sQuery(id+"F18.wireOp",EDGE,"E16")])]})}),makeQuery(id+"F35.opExtrude","SWEPT_FACE",FACE,{"disambiguationData":[OSD([subQ1])]}),makeQuery(id+"F35.opExtrude","SWEPT_FACE",FACE,{"disambiguationData":[OSD([subQ0])]})]),OD(0.0)],"derivedFrom":makeQuery(id+"F35.opExtrude","SWEPT_EDGE",EDGE,{"disambiguationData":[OSD([subQ1,subQ0])]})});}
            var Q10;
            {var subQ0=sQuery(id+"F34.wireOp",EDGE,"E36.bottom");var subQ1=sQuery(id+"F34.wireOp",EDGE,"E36.left");Q10=makeQuery(id+"F35.boolean.opBoolean","COPY",EDGE,{"disambiguationData":[TD([makeQuery(id+"F3.opExtrude","SWEPT_FACE",FACE,{"disambiguationData":[OSD([sQuery(id+"F0.wireOp",EDGE,"E7")])]}),makeQuery(id+"F13.boolean.opBoolean","COPY",FACE,{"derivedFrom":makeQuery(id+"F13.opExtrude","SWEPT_FACE",FACE,{"disambiguationData":[OSD([sQuery(id+"F12.wireOp",EDGE,"E13")])]})}),makeQuery(id+"F35.opExtrude","SWEPT_FACE",FACE,{"disambiguationData":[OSD([subQ0])]}),makeQuery(id+"F35.opExtrude","SWEPT_FACE",FACE,{"disambiguationData":[OSD([subQ1])]})]),OD(0.0)],"derivedFrom":makeQuery(id+"F35.opExtrude","SWEPT_EDGE",EDGE,{"disambiguationData":[OSD([subQ0,subQ1])]})});}
            var Q11;
            {var subQ0=sQuery(id+"F34.wireOp",EDGE,"E36.bottom");var subQ1=sQuery(id+"F34.wireOp",EDGE,"E36.left");Q11=makeQuery(id+"F35.boolean.opBoolean","COPY",EDGE,{"disambiguationData":[TD([makeQuery(id+"F3.opExtrude","SWEPT_FACE",FACE,{"disambiguationData":[OSD([sQuery(id+"F0.wireOp",EDGE,"E8")])]}),makeQuery(id+"F15.boolean.opBoolean","COPY",FACE,{"derivedFrom":makeQuery(id+"F15.opExtrude","SWEPT_FACE",FACE,{"disambiguationData":[OSD([sQuery(id+"F14.wireOp",EDGE,"E14")])]})}),makeQuery(id+"F35.opExtrude","SWEPT_FACE",FACE,{"disambiguationData":[OSD([subQ0])]}),makeQuery(id+"F35.opExtrude","SWEPT_FACE",FACE,{"disambiguationData":[OSD([subQ1])]})]),OD(0.0)],"derivedFrom":makeQuery(id+"F35.opExtrude","SWEPT_EDGE",EDGE,{"disambiguationData":[OSD([subQ0,subQ1])]})});}
            var Q12;
            {var subQ0=sQuery(id+"F34.wireOp",EDGE,"E36.top");var subQ1=sQuery(id+"F34.wireOp",EDGE,"E36.left");Q12=makeQuery(id+"F35.boolean.opBoolean","COPY",EDGE,{"disambiguationData":[TD([makeQuery(id+"F3.opExtrude","SWEPT_FACE",FACE,{"disambiguationData":[OSD([sQuery(id+"F0.wireOp",EDGE,"E7")])]}),makeQuery(id+"F13.boolean.opBoolean","COPY",FACE,{"derivedFrom":makeQuery(id+"F13.opExtrude","SWEPT_FACE",FACE,{"disambiguationData":[OSD([sQuery(id+"F12.wireOp",EDGE,"E13")])]})}),makeQuery(id+"F35.opExtrude","SWEPT_FACE",FACE,{"disambiguationData":[OSD([subQ0])]}),makeQuery(id+"F35.opExtrude","SWEPT_FACE",FACE,{"disambiguationData":[OSD([subQ1])]})]),OD(0.0)],"derivedFrom":makeQuery(id+"F35.opExtrude","SWEPT_EDGE",EDGE,{"disambiguationData":[OSD([subQ0,subQ1])]})});}
            var Q13;
            {var subQ0=sQuery(id+"F34.wireOp",EDGE,"E36.top");var subQ1=sQuery(id+"F34.wireOp",EDGE,"E36.left");Q13=makeQuery(id+"F35.boolean.opBoolean","COPY",EDGE,{"disambiguationData":[TD([makeQuery(id+"F3.opExtrude","SWEPT_FACE",FACE,{"disambiguationData":[OSD([sQuery(id+"F0.wireOp",EDGE,"E8")])]}),makeQuery(id+"F15.boolean.opBoolean","COPY",FACE,{"derivedFrom":makeQuery(id+"F15.opExtrude","SWEPT_FACE",FACE,{"disambiguationData":[OSD([sQuery(id+"F14.wireOp",EDGE,"E14")])]})}),makeQuery(id+"F35.opExtrude","SWEPT_FACE",FACE,{"disambiguationData":[OSD([subQ0])]}),makeQuery(id+"F35.opExtrude","SWEPT_FACE",FACE,{"disambiguationData":[OSD([subQ1])]})]),OD(0.0)],"derivedFrom":makeQuery(id+"F35.opExtrude","SWEPT_EDGE",EDGE,{"disambiguationData":[OSD([subQ0,subQ1])]})});}
            var Q14;
            {var subQ0=sQuery(id+"F34.wireOp",EDGE,"E35.bottom");var subQ1=sQuery(id+"F34.wireOp",EDGE,"E35.left");Q14=makeQuery(id+"F35.boolean.opBoolean","COPY",EDGE,{"disambiguationData":[TD([makeQuery(id+"F3.opExtrude","SWEPT_FACE",FACE,{"disambiguationData":[OSD([sQuery(id+"F0.wireOp",EDGE,"E8")])]}),makeQuery(id+"F17.boolean.opBoolean","COPY",FACE,{"derivedFrom":makeQuery(id+"F17.opExtrude","SWEPT_FACE",FACE,{"disambiguationData":[OSD([sQuery(id+"F16.wireOp",EDGE,"E15")])]})}),makeQuery(id+"F35.opExtrude","SWEPT_FACE",FACE,{"disambiguationData":[OSD([subQ0])]}),makeQuery(id+"F35.opExtrude","SWEPT_FACE",FACE,{"disambiguationData":[OSD([subQ1])]})]),OD(0.0)],"derivedFrom":makeQuery(id+"F35.opExtrude","SWEPT_EDGE",EDGE,{"disambiguationData":[OSD([subQ0,subQ1])]})});}
            var Q15;
            {var subQ0=sQuery(id+"F34.wireOp",EDGE,"E35.top");var subQ1=sQuery(id+"F34.wireOp",EDGE,"E35.left");Q15=makeQuery(id+"F35.boolean.opBoolean","COPY",EDGE,{"disambiguationData":[TD([makeQuery(id+"F3.opExtrude","SWEPT_FACE",FACE,{"disambiguationData":[OSD([sQuery(id+"F0.wireOp",EDGE,"E8")])]}),makeQuery(id+"F17.boolean.opBoolean","COPY",FACE,{"derivedFrom":makeQuery(id+"F17.opExtrude","SWEPT_FACE",FACE,{"disambiguationData":[OSD([sQuery(id+"F16.wireOp",EDGE,"E15")])]})}),makeQuery(id+"F35.opExtrude","SWEPT_FACE",FACE,{"disambiguationData":[OSD([subQ0])]}),makeQuery(id+"F35.opExtrude","SWEPT_FACE",FACE,{"disambiguationData":[OSD([subQ1])]})]),OD(0.0)],"derivedFrom":makeQuery(id+"F35.opExtrude","SWEPT_EDGE",EDGE,{"disambiguationData":[OSD([subQ0,subQ1])]})});}
            fillet(context, id + "F36", {"entities" : qUnion([Q0, Q1, Q2, Q3, Q4, Q5, Q6, Q7, Q8, Q9, Q10, Q11, Q12, Q13, Q14, Q15]), "radius" : 0.4 * mm, "tangentPropagation" : true, "allowEdgeOverflow" : false});
        }
        {
            var Q0;
            {var subQ0=sQuery(id+"F10.wireOp",EDGE,"E12");Q0=makeQuery(id+"F35.boolean.opBoolean","SPLIT",FACE,{"disambiguationData":[TD([makeQuery(id+"F35.opExtrude","SWEPT_FACE",FACE,{"disambiguationData":[OSD([sQuery(id+"F34.wireOp",EDGE,"E36.top")])]})])],"derivedFrom":makeQuery(id+"F11.opExtrude","CAP_FACE",FACE,{"disambiguationData":[OSD([subQ0])],"isStart":true})});}
            var Q1;
            {var subQ0=sQuery(id+"F10.wireOp",EDGE,"E12");Q1=makeQuery(id+"F35.boolean.opBoolean","SPLIT",FACE,{"disambiguationData":[TD([makeQuery(id+"F35.opExtrude","SWEPT_FACE",FACE,{"disambiguationData":[OSD([sQuery(id+"F34.wireOp",EDGE,"E36.bottom")])]})])],"derivedFrom":makeQuery(id+"F11.opExtrude","CAP_FACE",FACE,{"disambiguationData":[OSD([subQ0])],"isStart":true})});}
            var Q2;
            {var subQ0=sQuery(id+"F8.wireOp",EDGE,"E11");Q2=makeQuery(id+"F35.boolean.opBoolean","SPLIT",FACE,{"disambiguationData":[TD([makeQuery(id+"F35.opExtrude","SWEPT_FACE",FACE,{"disambiguationData":[OSD([sQuery(id+"F34.wireOp",EDGE,"E36.top")])]})])],"derivedFrom":makeQuery(id+"F9.opExtrude","CAP_FACE",FACE,{"disambiguationData":[OSD([subQ0])],"isStart":true})});}
            var Q3;
            {var subQ0=sQuery(id+"F8.wireOp",EDGE,"E11");Q3=makeQuery(id+"F35.boolean.opBoolean","SPLIT",FACE,{"disambiguationData":[TD([makeQuery(id+"F35.opExtrude","SWEPT_FACE",FACE,{"disambiguationData":[OSD([sQuery(id+"F34.wireOp",EDGE,"E36.bottom")])]})])],"derivedFrom":makeQuery(id+"F9.opExtrude","CAP_FACE",FACE,{"disambiguationData":[OSD([subQ0])],"isStart":true})});}
            extrude(context, id + "F37", {"entities" : qUnion([Q0, Q1, Q2, Q3]), "operationType" : NewBodyOperationType.REMOVE, "oppositeDirection" : true, "depth" : 0.1 * mm, "offsetDistance" : 25 * mm});
        }
        {
            var Q0;
            {var subQ0=sQuery(id+"F4.wireOp",EDGE,"E9");Q0=makeQuery(id+"F35.boolean.opBoolean","SPLIT",FACE,{"disambiguationData":[TD([makeQuery(id+"F35.opExtrude","SWEPT_FACE",FACE,{"disambiguationData":[OSD([sQuery(id+"F34.wireOp",EDGE,"E35.bottom")])]})])],"derivedFrom":makeQuery(id+"F5.opExtrude","CAP_FACE",FACE,{"disambiguationData":[OSD([subQ0])],"isStart":true})});}
            var Q1;
            {var subQ0=sQuery(id+"F4.wireOp",EDGE,"E9");Q1=makeQuery(id+"F35.boolean.opBoolean","SPLIT",FACE,{"disambiguationData":[TD([makeQuery(id+"F35.opExtrude","SWEPT_FACE",FACE,{"disambiguationData":[OSD([sQuery(id+"F34.wireOp",EDGE,"E35.top")])]})])],"derivedFrom":makeQuery(id+"F5.opExtrude","CAP_FACE",FACE,{"disambiguationData":[OSD([subQ0])],"isStart":true})});}
            var Q2;
            {var subQ0=sQuery(id+"F6.wireOp",EDGE,"E10");Q2=makeQuery(id+"F35.boolean.opBoolean","SPLIT",FACE,{"disambiguationData":[TD([makeQuery(id+"F35.opExtrude","SWEPT_FACE",FACE,{"disambiguationData":[OSD([sQuery(id+"F34.wireOp",EDGE,"E35.bottom")])]})])],"derivedFrom":makeQuery(id+"F7.opExtrude","CAP_FACE",FACE,{"disambiguationData":[OSD([subQ0])],"isStart":true})});}
            var Q3;
            {var subQ0=sQuery(id+"F6.wireOp",EDGE,"E10");Q3=makeQuery(id+"F35.boolean.opBoolean","SPLIT",FACE,{"disambiguationData":[TD([makeQuery(id+"F35.opExtrude","SWEPT_FACE",FACE,{"disambiguationData":[OSD([sQuery(id+"F34.wireOp",EDGE,"E35.top")])]})])],"derivedFrom":makeQuery(id+"F7.opExtrude","CAP_FACE",FACE,{"disambiguationData":[OSD([subQ0])],"isStart":true})});}
            extrude(context, id + "F38", {"entities" : qUnion([Q0, Q1, Q2, Q3]), "operationType" : NewBodyOperationType.REMOVE, "oppositeDirection" : true, "depth" : 0.1 * mm, "offsetDistance" : 25 * mm});
        }
    });
